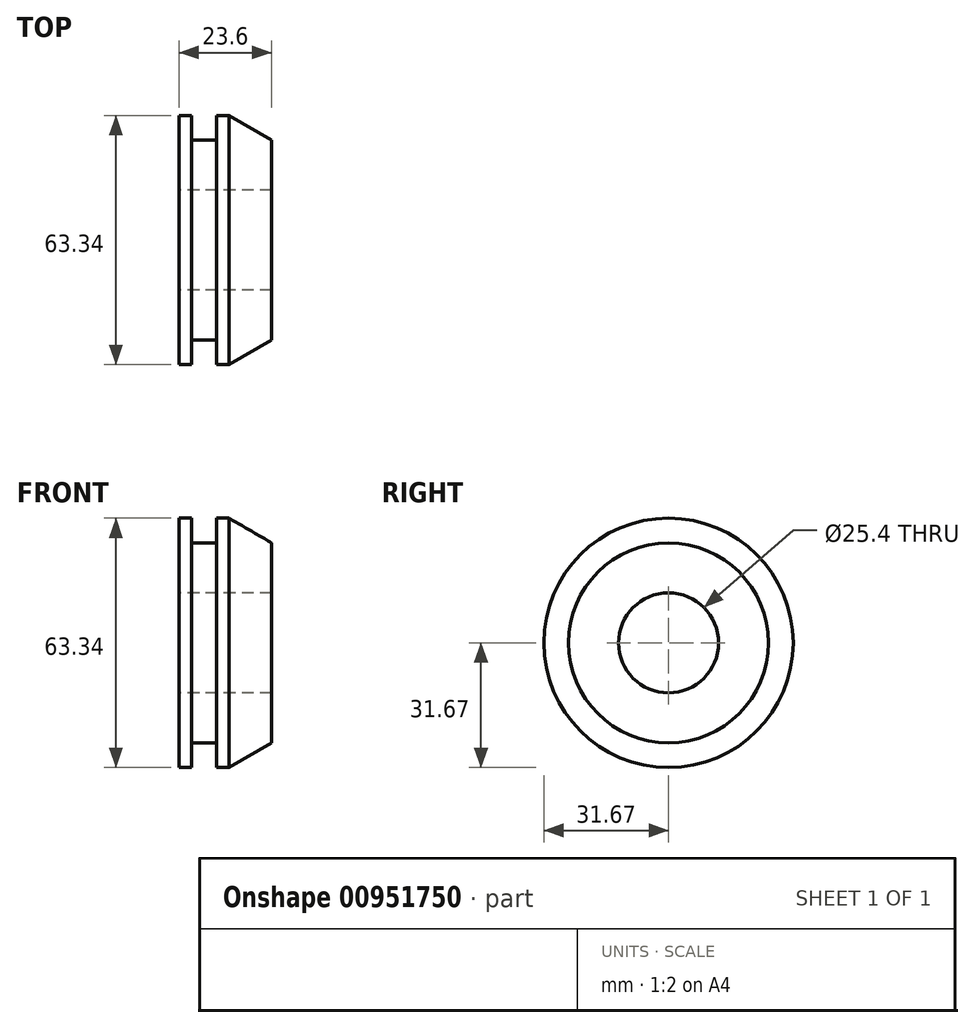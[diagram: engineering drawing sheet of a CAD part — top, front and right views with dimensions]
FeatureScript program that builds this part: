
annotation { "Feature Type Name" : "Feature", "Feature Type Description" : "" }
export const myFeature = defineFeature(function(context is Context, id is Id, definition is map)
    precondition{}
    {
        {
            var Q0;
            Q0=qCreatedBy(makeId("Front.planeOp"),FACE);
            var sketch = newSketch(context, id + "F0", { "sketchPlane" : qUnion([Q0])});
            skLineSegment(sketch, "E0", {"start": v(0, 31.67) * mm, "end": v(3.2, 31.67) * mm});
            skLineSegment(sketch, "E1", {"start": v(3.2, 31.67) * mm, "end": v(3.2, 25.4) * mm});
            skLineSegment(sketch, "E2", {"start": v(3.2, 25.4) * mm, "end": v(9.54, 25.4) * mm});
            skLineSegment(sketch, "E3", {"start": v(9.54, 25.4) * mm, "end": v(9.54, 31.67) * mm});
            skLineSegment(sketch, "E4", {"start": v(9.54, 31.67) * mm, "end": v(12.73, 31.67) * mm});
            skLineSegment(sketch, "E5", {"start": v(12.73, 31.67) * mm, "end": v(23.6, 25.4) * mm});
            skLineSegment(sketch, "E6", {"start": v(23.6, 25.4) * mm, "end": v(23.6, 12.7) * mm});
            skLineSegment(sketch, "E7", {"start": v(23.6, 12.7) * mm, "end": v(0, 12.7) * mm});
            skLineSegment(sketch, "E8", {"start": v(0, 12.7) * mm, "end": v(0, 31.67) * mm});
            skLineSegment(sketch, "E9", {"start": v(0, 0) * mm, "end": v(93.37, 0) * mm, "construction": true});
            skSolve(sketch);
        }
        {
            var Q0;
            Q0=makeQuery(id+"F0.imprint","IMPRINT",FACE,{"disambiguationData":[TD([[makeQuery(id+"F0.imprint","IMPRINT",EDGE,{"derivedFrom":sQuery(id+"F0.wireOp",EDGE,"E0")}),-1.0]])]});
            var Q1;
            Q1=sQuery(id+"F0.wireOp",EDGE,"E9");
            var Q2;
            Q2=sQuery(id+"F0.wireOp",EDGE,"E9");
            revolve(context, id + "F1", {"surfaceOperationType" : NewSurfaceOperationType.NEW, "entities" : qUnion([Q0]), "surfaceEntities" : qUnion([Q1]), "axis" : qUnion([Q2]), "revolveType" : RevolveType.FULL});
        }
    });
